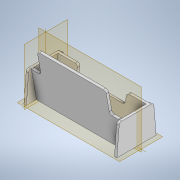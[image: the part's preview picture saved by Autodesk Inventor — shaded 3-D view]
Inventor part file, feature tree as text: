
AUTODESK INVENTOR PART (.ipt)
format: ipt  version: 2021 (Build 250183000, 183)  size: 205,312 bytes
history: native  units: mm
features: extrude x4, sketch x4, fillet x1, mirror x1
ambient origin geometry x8: Origin, YZ Plane, XZ Plane, XY Plane, X Axis, Y Axis, Z Axis, Center Point
bodies: Solid1 (feature_tree)
feature tree (10):
  extrude  "Extrusion1"  Depth=35.0mm
  extrude  "Extrusion2"  TaperAngle=0.0deg  [1 undecoded]
  extrude  "Extrusion5"  Depth=2.5mm
  extrude  "Extrusion6"  Depth=2.5mm
  fillet  "Fillet1"  Radius=2.5mm
  mirror  "Mirror1"
  sketch  "Sketch2"  dims[d4=30.0mm d5=35.0mm]
  sketch  "Sketch5"  dims[d6=40.0mm d14=0.0mm]
  sketch  "Sketch8"  dims[d15=2.5mm d16=2.5mm]
  sketch  "Sketch9"  dims[d17=2.5mm d18=2.5mm d19=2.5mm d20=50.0mm d22=17.453293mm d23=17.453293mm d24=45.0mm d25=0.0mm d33=10.0mm d34=25.0mm d35=2.5mm d36=0.0mm d38=10.0mm d39=2.5mm d40=0.0mm d41=2.5mm]
note: 1 required parameter value undecoded (feature->parameter linkage not recoverable at this tier; creation-order binding heuristic only, values carry confidence <= 0.55)
